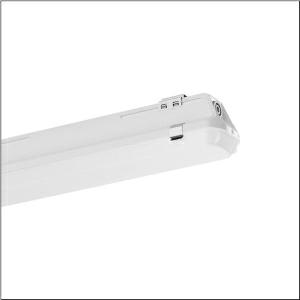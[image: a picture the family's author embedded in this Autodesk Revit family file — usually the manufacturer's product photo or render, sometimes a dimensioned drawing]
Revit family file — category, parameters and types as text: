
# Revit family: monsun_r__11_51fp20fp460h_df5a
name_source: partatom
category: Lighting Fixtures
units: mm (PartAtom-declared; Revit-internal decimal feet)

## family parameters
Cut with Voids When Loaded = No
Host = Face
Light Source = No
Part Type = Normal
Room Calculation Point = No
Round Connector Dimension = Use Diameter
Shared = No

## types (1)
- --- (1 x LED, 5450 lm, 34.6 W, 4000K)
    Apparent Load = 35 VA
    CIE Flux Codes = 45 75 93 94 100
    Color Rendering = 80
    Color Temperature = 4000K
    Default Elevation = 1800 mm
    Description = Monsun® 11, damp-proof luminaire, chain hanger, primary optical cover: enclosure, of PC, light emission: direct distribution, primary light characteristic: symmetric, installation type: suspended mounting, surface-mounted, horizontal mounting, vertical mounting, LED, rated luminous flux: 5.450lm, luminous efficacy: 158lm/W, light colour: 840, colour temperature: 4000K, control gear: ECG DALI, with terminal, 5-pole, max. 2.5mm², mains connection: 220..240V, AC, 50/60Hz, start of lifetime: 35W, end of service life: 39W, luminaire housing, of glass-fibre reinforced polyester, uncoated, bright grey, incl. chain hanger, length: 1.590mm, width: 90mm, height: 88mm, clip for enclosure, of stainless steel (V2A), ceiling mounting element, of stainless steel (V2A), chain hanger, of stainless steel (V2A), protection rating (complete): IP66, insulation class (complete): insulation class I (protective earthing), certification: CE, ENEC, VDE, UKCA, protection symbol: D, impact resistance: IK08, permissible operating ambient temperature: -25..+40°C, standard: EN 50419, EN 60598-2-1, no direct snow, no direct sun, no direct rain, for indoor or canopied outdoor use, corresponds to IFS (International Featured Standards) requirements for safety and quality in the food industry, contact your sales advisor before using the luminaires in applications with unclear chemical exposure, large temperature fluctuations or condensation-forming humidity, LABS conformity tested according to VDMA 24364:2018-05, packaging unit: 1 piece
    Height = 89 mm
    Lamp = 1 x LED
    Lamp Light Flux = 5450 lm
    Lamp Power = 34.6 W
    Lamp count = 1
    Length = 1590 mm
    Luminous efficacy = 158 lm/W
    Manufacturer = Siteco
    ModVariant = No
    Model = 51FP20FP460H
    Mounting Place = Ceiling
    Mounting Type = Surface mounted
    Number of Poles = 1
    OnlyDefault = Yes
    Power Factor = 1
    Product Name = Monsun® 11
    Product group = damp-proof luminaire
    ProductGroupID = 301
    Protection Class = Protection class I
    Protection Degree = IP 66
    RLX_Detail_Level = 1
    RLX_Emergency_Light_Flux = 0 lm
    RLX_Emergency_Type = 0
    RLX_Emergency_Type_DB = No
    RlxData = <blob elided: 92097 chars, md5=5e37c5da>
    Socket = socket
    Standby Power = 0 W
    System Light Flux = 5450 lm
    System Power = 35 W
    Type Comments = factory setting: luminous flux: 100 % | dim-lin: 254 | 232 mA
    Type Image = l_1004748.jpg
    URL = http://relux.com
    VarID = @adj_156347
    Voltage = 0 V
    Weight = 0.00 kg
    Width = 90 mm

## geometry (parser evidence)
native form markers: Blend x4, Sweep x13
no freeform markers — native parametric forms only
